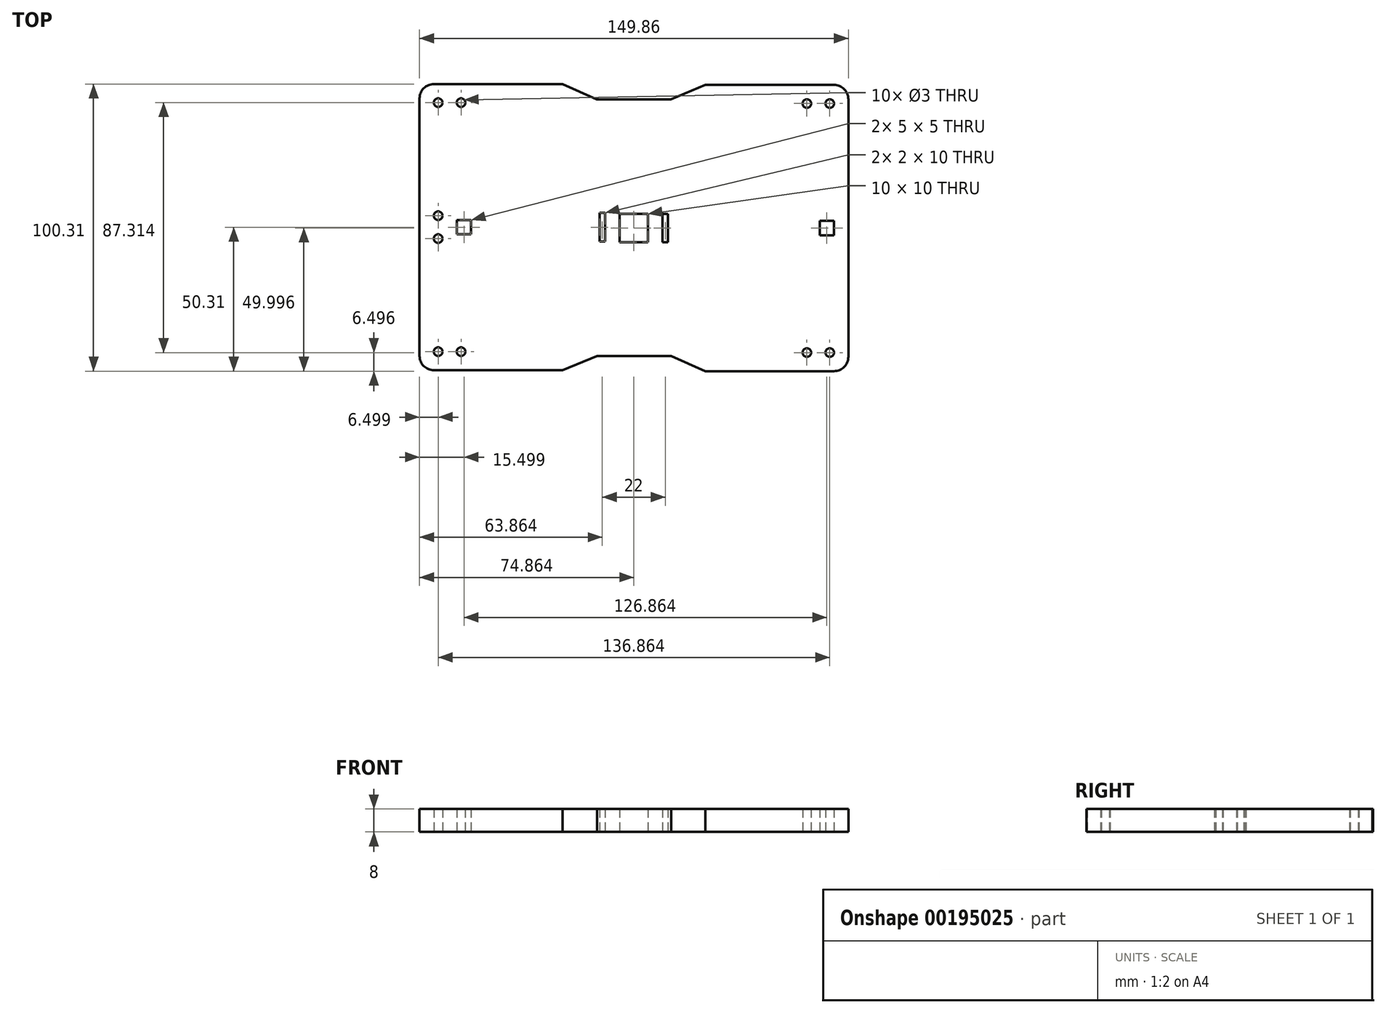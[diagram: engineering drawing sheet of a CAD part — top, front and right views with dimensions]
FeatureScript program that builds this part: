
annotation { "Feature Type Name" : "Feature", "Feature Type Description" : "" }
export const myFeature = defineFeature(function(context is Context, id is Id, definition is map)
    precondition{}
    {
        {
            var Q0;
            Q0=qCreatedBy(makeId("Top.planeOp"),FACE);
            var sketch = newSketch(context, id + "F0", { "sketchPlane" : qUnion([Q0])});
            skLineSegment(sketch, "E0", {"start": v(-75.6, 54) * mm, "end": v(-75.6, -46) * mm});
            skLineSegment(sketch, "E1", {"start": v(-75.6, 54) * mm, "end": v(-25.6, 54) * mm});
            skLineSegment(sketch, "E2", {"start": v(24.27, 53.69) * mm, "end": v(74.27, 53.69) * mm});
            skLineSegment(sketch, "E3", {"start": v(74.27, 53.69) * mm, "end": v(74.27, -46.31) * mm});
            skLineSegment(sketch, "E4", {"start": v(-75.6, -46) * mm, "end": v(-25.6, -46) * mm});
            skLineSegment(sketch, "E5", {"start": v(74.27, -46.31) * mm, "end": v(24.27, -46.31) * mm});
            skLineSegment(sketch, "E6", {"start": v(-13.73, 48.69) * mm, "end": v(12.27, 48.69) * mm});
            skLineSegment(sketch, "E7", {"start": v(-25.6, 54) * mm, "end": v(-13.73, 48.69) * mm});
            skLineSegment(sketch, "E8", {"start": v(24.27, 53.69) * mm, "end": v(12.27, 48.69) * mm});
            skLineSegment(sketch, "E9", {"start": v(-13.6, -41) * mm, "end": v(12.4, -41) * mm});
            skLineSegment(sketch, "E10", {"start": v(24.27, -46.31) * mm, "end": v(12.4, -41) * mm});
            skLineSegment(sketch, "E11", {"start": v(-25.6, -46) * mm, "end": v(-13.6, -41) * mm});
            skCircle(sketch, "E12", {"center": v(67.77, 47.19) * mm, "radius": 1.5 * mm});
            skCircle(sketch, "E13", {"center": v(59.77, 47.19) * mm, "radius": 1.5 * mm});
            skCircle(sketch, "E14", {"center": v(67.77, -39.81) * mm, "radius": 1.5 * mm});
            skCircle(sketch, "E15", {"center": v(59.77, -39.81) * mm, "radius": 1.5 * mm});
            skCircle(sketch, "E16", {"center": v(-69.1, -39.5) * mm, "radius": 1.5 * mm});
            skCircle(sketch, "E17", {"center": v(-61.1, -39.5) * mm, "radius": 1.5 * mm});
            skCircle(sketch, "E18", {"center": v(-69.1, 47.5) * mm, "radius": 1.5 * mm});
            skCircle(sketch, "E19", {"center": v(-61.1, 47.5) * mm, "radius": 1.5 * mm});
            skCircle(sketch, "E20", {"center": v(-69.1, 8) * mm, "radius": 1.5 * mm});
            skCircle(sketch, "E21", {"center": v(-69.1, 0) * mm, "radius": 1.5 * mm});
            skLineSegment(sketch, "E22", {"start": v(-62.6, 6.5) * mm, "end": v(-62.6, 1.5) * mm});
            skLineSegment(sketch, "E23", {"start": v(-62.6, 6.5) * mm, "end": v(-57.6, 6.5) * mm});
            skLineSegment(sketch, "E24", {"start": v(-62.6, 1.5) * mm, "end": v(-57.6, 1.5) * mm});
            skLineSegment(sketch, "E25", {"start": v(-57.6, 1.5) * mm, "end": v(-57.6, 6.5) * mm});
            skLineSegment(sketch, "E26", {"start": v(-5.73, 8.69) * mm, "end": v(-5.73, -1.31) * mm});
            skLineSegment(sketch, "E27", {"start": v(-5.73, 8.69) * mm, "end": v(4.27, 8.69) * mm});
            skLineSegment(sketch, "E28", {"start": v(4.27, 8.69) * mm, "end": v(4.27, -1.31) * mm});
            skLineSegment(sketch, "E29", {"start": v(4.27, -1.31) * mm, "end": v(-5.73, -1.31) * mm});
            skLineSegment(sketch, "E30.bottom", {"start": v(-12.73, 9) * mm, "end": v(-10.73, 9) * mm});
            skLineSegment(sketch, "E30.top", {"start": v(-12.73, -1) * mm, "end": v(-10.73, -1) * mm});
            skLineSegment(sketch, "E30.left", {"start": v(-12.73, 9) * mm, "end": v(-12.73, -1) * mm});
            skLineSegment(sketch, "E30.right", {"start": v(-10.73, 9) * mm, "end": v(-10.73, -1) * mm});
            skLineSegment(sketch, "E31.bottom", {"start": v(9.27, 8.69) * mm, "end": v(11.27, 8.69) * mm});
            skLineSegment(sketch, "E31.top", {"start": v(9.27, -1.31) * mm, "end": v(11.27, -1.31) * mm});
            skLineSegment(sketch, "E31.left", {"start": v(9.27, 8.69) * mm, "end": v(9.27, -1.31) * mm});
            skLineSegment(sketch, "E31.right", {"start": v(11.27, 8.69) * mm, "end": v(11.27, -1.31) * mm});
            skLineSegment(sketch, "E32.bottom", {"start": v(64.27, 6.19) * mm, "end": v(69.27, 6.19) * mm});
            skLineSegment(sketch, "E32.top", {"start": v(64.27, 1.19) * mm, "end": v(69.27, 1.19) * mm});
            skLineSegment(sketch, "E32.left", {"start": v(64.27, 6.19) * mm, "end": v(64.27, 1.19) * mm});
            skLineSegment(sketch, "E32.right", {"start": v(69.27, 6.19) * mm, "end": v(69.27, 1.19) * mm});
            skSolve(sketch);
        }
        {
            var Q0;
            Q0=makeQuery(id+"F0.imprint","IMPRINT",FACE,{"disambiguationData":[TD([[makeQuery(id+"F0.imprint","IMPRINT",EDGE,{"derivedFrom":sQuery(id+"F0.wireOp",EDGE,"E0")}),1.0]])]});
            extrude(context, id + "F1", {"entities" : qUnion([Q0]), "endBound" : BoundingType.SYMMETRIC, "depth" : 8 * mm});
        }
        {
            var Q0;
            Q0=makeQuery(id+"F1.opExtrude","SWEPT_EDGE",EDGE,{"disambiguationData":[OSD([sQuery(id+"F0.wireOp",EDGE,"E0"),sQuery(id+"F0.wireOp",EDGE,"E1")])]});
            var Q1;
            Q1=makeQuery(id+"F1.opExtrude","SWEPT_EDGE",EDGE,{"disambiguationData":[OSD([sQuery(id+"F0.wireOp",EDGE,"E2"),sQuery(id+"F0.wireOp",EDGE,"E3")])]});
            var Q2;
            Q2=makeQuery(id+"F1.opExtrude","SWEPT_EDGE",EDGE,{"disambiguationData":[OSD([sQuery(id+"F0.wireOp",EDGE,"E3"),sQuery(id+"F0.wireOp",EDGE,"E5")])]});
            var Q3;
            Q3=makeQuery(id+"F1.opExtrude","SWEPT_EDGE",EDGE,{"disambiguationData":[OSD([sQuery(id+"F0.wireOp",EDGE,"E0"),sQuery(id+"F0.wireOp",EDGE,"E4")])]});
            fillet(context, id + "F2", {"entities" : qUnion([Q0, Q1, Q2, Q3]), "radius" : 5 * mm, "tangentPropagation" : true, "allowEdgeOverflow" : false});
        }
    });
